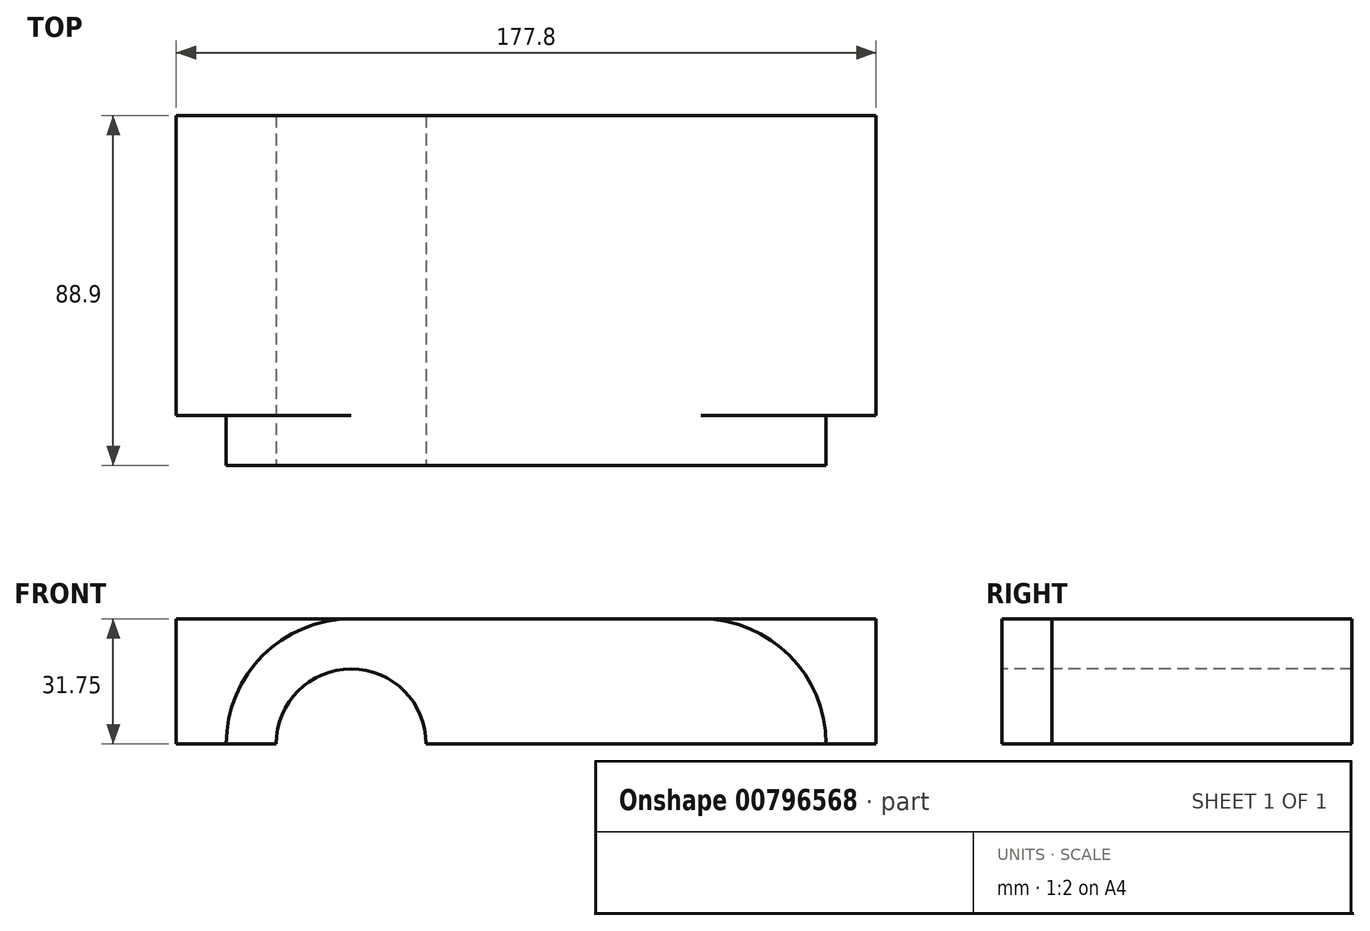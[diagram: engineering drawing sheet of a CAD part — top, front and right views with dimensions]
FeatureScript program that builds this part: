
annotation { "Feature Type Name" : "Feature", "Feature Type Description" : "" }
export const myFeature = defineFeature(function(context is Context, id is Id, definition is map)
    precondition{}
    {
        {
            var Q0;
            Q0=qCreatedBy(makeId("Front.planeOp"),FACE);
            var sketch = newSketch(context, id + "F0", { "sketchPlane" : qUnion([Q0])});
            skLineSegment(sketch, "E0.bottom", {"start": v(88.9, 0) * mm, "end": v(-88.9, 0) * mm});
            skLineSegment(sketch, "E0.top", {"start": v(88.9, 31.75) * mm, "end": v(-88.9, 31.75) * mm});
            skLineSegment(sketch, "E0.left", {"start": v(88.9, 0) * mm, "end": v(88.9, 31.75) * mm});
            skLineSegment(sketch, "E0.right", {"start": v(-88.9, 0) * mm, "end": v(-88.9, 31.75) * mm});
            skPoint(sketch, "E0.middle", {"position": v(0, 15.88) * mm});
            skSolve(sketch);
        }
        {
            var Q0;
            Q0 = qSketchRegion(id + "F0", true);
            extrude(context, id + "F1", {"entities" : qUnion([Q0]), "endBound" : BoundingType.SYMMETRIC, "depth" : 76.2 * mm, "offsetDistance" : 25.4 * mm});
        }
        {
            var Q0;
            Q0=makeQuery(id+"F1.opExtrude","CAP_FACE",FACE,{"disambiguationData":[OSD([sQuery(id+"F0.wireOp",EDGE,"E0.bottom"),sQuery(id+"F0.wireOp",EDGE,"E0.top"),sQuery(id+"F0.wireOp",EDGE,"E0.left"),sQuery(id+"F0.wireOp",EDGE,"E0.right")])],"isStart":false});
            var sketch = newSketch(context, id + "F2", { "sketchPlane" : qUnion([Q0])});
            skArc(sketch, "E1", {"start": v(44.45, 31.75) * mm, "mid": v(66.9, 22.45) * mm, "end": v(76.2, 0) * mm});
            skLineSegment(sketch, "E2", {"start": v(-44.45, 31.75) * mm, "end": v(44.45, 31.75) * mm});
            skLineSegment(sketch, "E3", {"start": v(76.2, 0) * mm, "end": v(-76.2, 0) * mm});
            skArc(sketch, "E4.MirrorCS", {"start": v(-44.45, 31.75) * mm, "mid": v(-66.9, 22.45) * mm, "end": v(-76.2, 0) * mm});
            skSolve(sketch);
        }
        {
            var Q0;
            Q0 = qSketchRegion(id + "F2", true);
            extrude(context, id + "F3", {"entities" : qUnion([Q0]), "operationType" : NewBodyOperationType.ADD, "depth" : 12.7 * mm, "offsetDistance" : 25.4 * mm});
        }
        {
            var Q0;
            Q0=makeQuery(id+"F3.opExtrude","CAP_FACE",FACE,{"disambiguationData":[OSD([sQuery(id+"F2.wireOp",EDGE,"E1"),sQuery(id+"F2.wireOp",EDGE,"E2"),sQuery(id+"F2.wireOp",EDGE,"E3"),sQuery(id+"F2.wireOp",EDGE,"E4.MirrorCS")])],"isStart":false});
            var sketch = newSketch(context, id + "F4", { "sketchPlane" : qUnion([Q0])});
            skArc(sketch, "E5", {"start": v(-25.4, 0) * mm, "mid": v(-44.45, 19.05) * mm, "end": v(-63.5, 0) * mm});
            skLineSegment(sketch, "E6", {"start": v(-63.5, 0) * mm, "end": v(-25.4, 0) * mm});
            skSolve(sketch);
        }
        {
            var Q0;
            Q0 = qSketchRegion(id + "F4", true);
            extrude(context, id + "F5", {"entities" : qUnion([Q0]), "operationType" : NewBodyOperationType.REMOVE, "endBound" : BoundingType.THROUGH_ALL, "oppositeDirection" : true, "depth" : 25.4 * mm, "offsetDistance" : 25.4 * mm});
        }
    });
